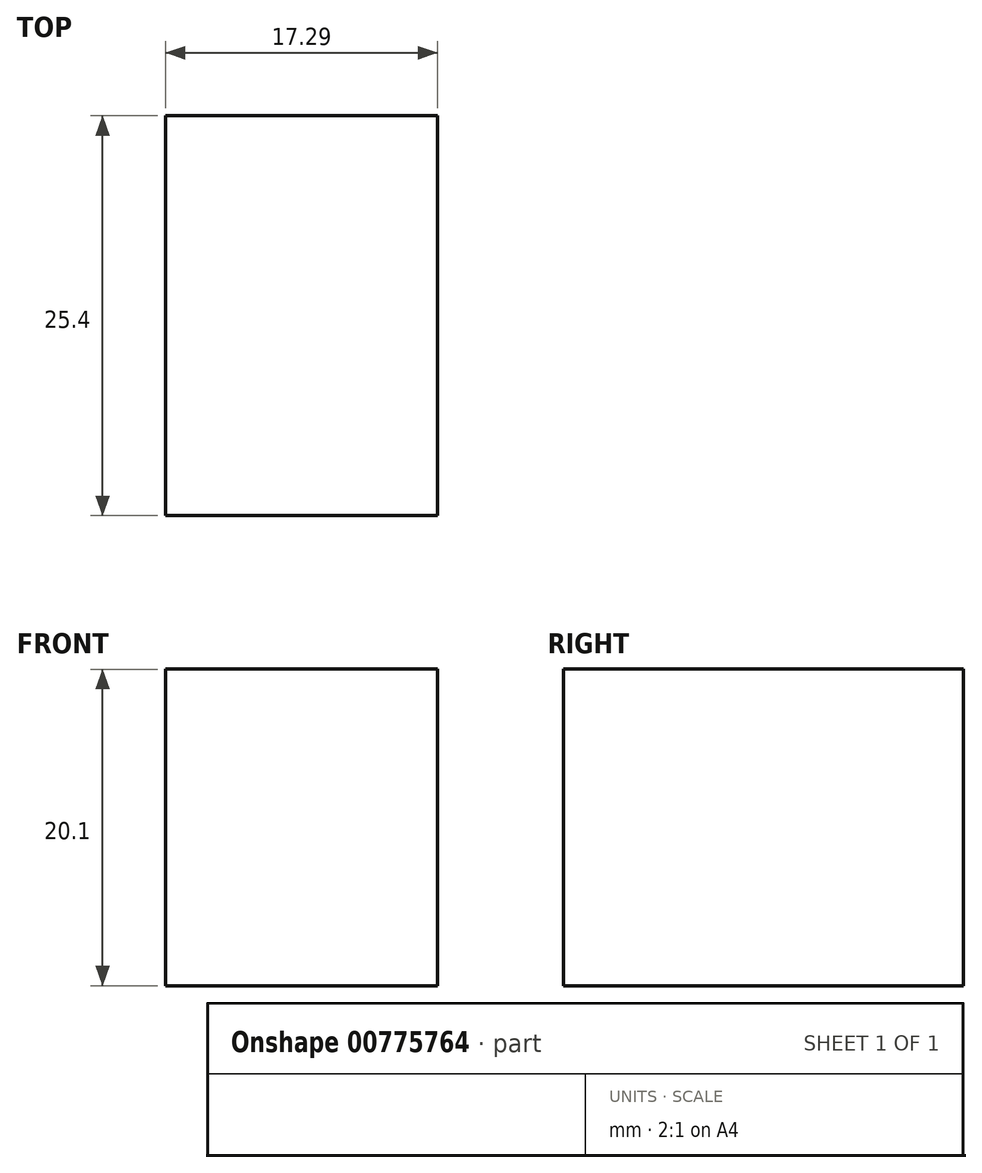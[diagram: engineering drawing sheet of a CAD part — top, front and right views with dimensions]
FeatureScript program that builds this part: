
annotation { "Feature Type Name" : "Feature", "Feature Type Description" : "" }
export const myFeature = defineFeature(function(context is Context, id is Id, definition is map)
    precondition{}
    {
        {
            var Q0;
            Q0=qCreatedBy(makeId("Front.planeOp"),FACE);
            var sketch = newSketch(context, id + "F0", { "sketchPlane" : qUnion([Q0])});
            skLineSegment(sketch, "E0.bottom", {"start": v(-53.07, 64.54) * mm, "end": v(-35.78, 64.54) * mm});
            skLineSegment(sketch, "E0.top", {"start": v(-53.07, 44.44) * mm, "end": v(-35.78, 44.44) * mm});
            skLineSegment(sketch, "E0.left", {"start": v(-53.07, 64.54) * mm, "end": v(-53.07, 44.44) * mm});
            skLineSegment(sketch, "E0.right", {"start": v(-35.78, 64.54) * mm, "end": v(-35.78, 44.44) * mm});
            skSolve(sketch);
        }
        {
            var Q0;
            Q0 = qSketchRegion(id + "F0", true);
            extrude(context, id + "F1", {"entities" : qUnion([Q0]), "depth" : 25.4 * mm, "offsetDistance" : 25.4 * mm});
        }
    });
